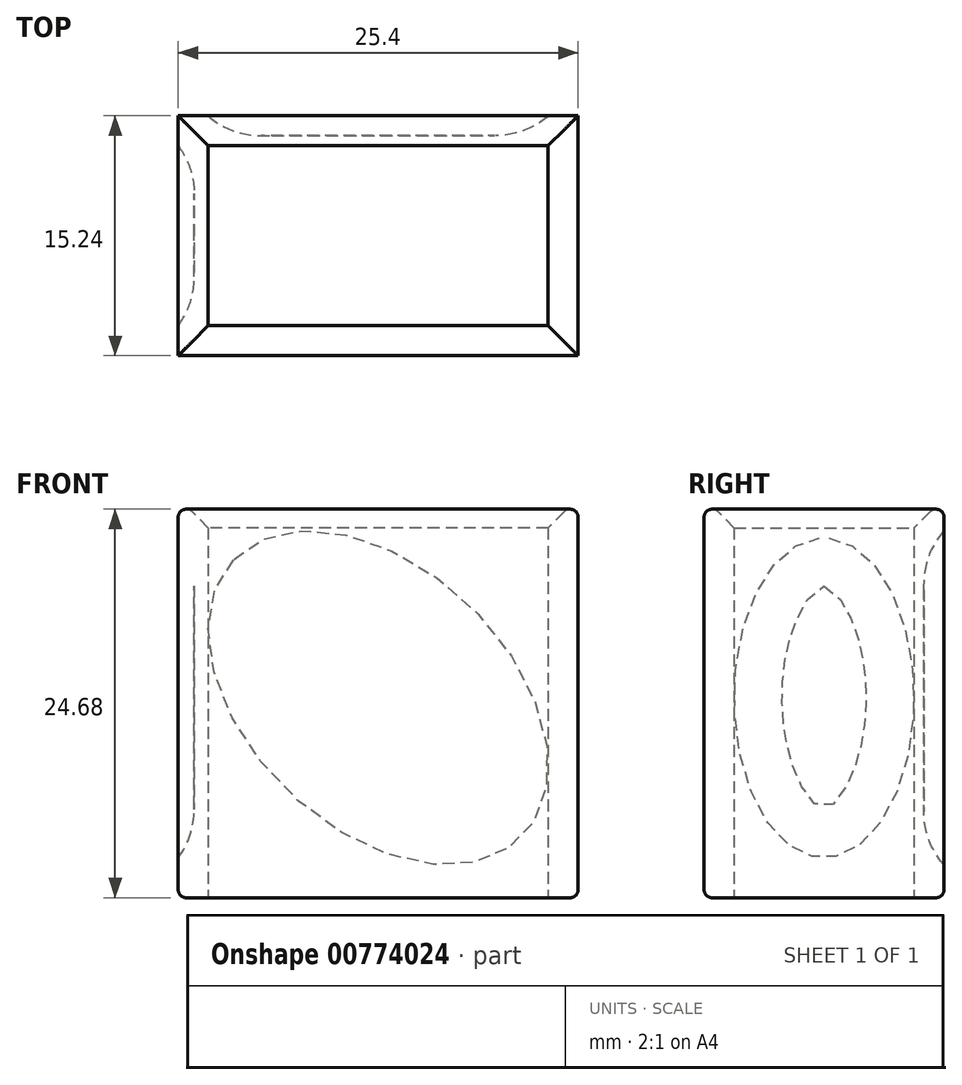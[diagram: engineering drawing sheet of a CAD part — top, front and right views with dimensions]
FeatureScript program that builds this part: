
annotation { "Feature Type Name" : "Feature", "Feature Type Description" : "" }
export const myFeature = defineFeature(function(context is Context, id is Id, definition is map)
    precondition{}
    {
        {
            var Q0;
            Q0=qCreatedBy(makeId("Top.planeOp"),FACE);
            var sketch = newSketch(context, id + "F0", { "sketchPlane" : qUnion([Q0])});
            skLineSegment(sketch, "E0.bottom", {"start": v(10.8, 5.72) * mm, "end": v(-10.8, 5.72) * mm});
            skLineSegment(sketch, "E0.top", {"start": v(10.8, -5.71) * mm, "end": v(-10.8, -5.71) * mm});
            skLineSegment(sketch, "E0.left", {"start": v(10.8, 5.72) * mm, "end": v(10.8, -5.71) * mm});
            skLineSegment(sketch, "E0.right", {"start": v(-10.8, 5.72) * mm, "end": v(-10.8, -5.72) * mm});
            skPoint(sketch, "E0.middle", {"position": v(0, 0) * mm});
            skLineSegment(sketch, "E1.0", {"start": v(12.7, 7.62) * mm, "end": v(-12.7, 7.62) * mm});
            skLineSegment(sketch, "E1.1", {"start": v(12.7, 7.62) * mm, "end": v(12.7, -7.62) * mm});
            skLineSegment(sketch, "E1.2", {"start": v(12.7, -7.62) * mm, "end": v(-12.7, -7.62) * mm});
            skLineSegment(sketch, "E1.3", {"start": v(-12.7, 7.62) * mm, "end": v(-12.7, -7.62) * mm});
            skSolve(sketch);
        }
        {
            var Q0;
            Q0=makeQuery(id+"F0.imprint","IMPRINT",FACE,{"disambiguationData":[TD([[makeQuery(id+"F0.imprint","IMPRINT",EDGE,{"derivedFrom":sQuery(id+"F0.wireOp",EDGE,"E0.bottom")}),-1.0]])]});
            extrude(context, id + "F1", {"entities" : qUnion([Q0]), "depth" : 25.4 * mm, "offsetDistance" : 25.4 * mm});
        }
        {
            var Q0;
            Q0=makeQuery(id+"F1.opExtrude","CAP_EDGE",EDGE,{"disambiguationData":[OSD([sQuery(id+"F0.wireOp",EDGE,"E0.right")])],"isStart":false});
            var Q1;
            Q1=makeQuery(id+"F1.opExtrude","CAP_EDGE",EDGE,{"disambiguationData":[OSD([sQuery(id+"F0.wireOp",EDGE,"E0.bottom")])],"isStart":false});
            var Q2;
            Q2=makeQuery(id+"F1.opExtrude","CAP_EDGE",EDGE,{"disambiguationData":[OSD([sQuery(id+"F0.wireOp",EDGE,"E0.top")])],"isStart":false});
            var Q3;
            Q3=makeQuery(id+"F1.opExtrude","CAP_EDGE",EDGE,{"disambiguationData":[OSD([sQuery(id+"F0.wireOp",EDGE,"E0.left")])],"isStart":false});
            chamfer(context, id + "F2", {"entities" : qUnion([Q0, Q1, Q2, Q3]), "width" : 1.9 * mm, "tangentPropagation" : true});
        }
        {
            var Q0;
            Q0=makeQuery(id+"F1.opExtrude","SWEPT_FACE",FACE,{"disambiguationData":[OSD([sQuery(id+"F0.wireOp",EDGE,"E1.3")])]});
            var sketch = newSketch(context, id + "F3", { "sketchPlane" : qUnion([Q0])});
            skEllipse(sketch, "E2", {"center": v(0, 12.7) * mm, "majorRadius": 10.16 * mm, "minorRadius": 5.72 * mm, "majorAxis": v(0, 1)});
            skPoint(sketch, "E3.orphan", {"position": v(-7.62, 12.7) * mm});
            skSolve(sketch);
        }
        {
            var Q0;
            Q0=makeQuery(id+"F3.imprint","IMPRINT",FACE,{"disambiguationData":[TD([[makeQuery(id+"F3.imprint","IMPRINT",EDGE,{"derivedFrom":sQuery(id+"F3.wireOp",EDGE,"E2")}),1.0]])]});
            extrude(context, id + "F4", {"entities" : qUnion([Q0]), "operationType" : NewBodyOperationType.REMOVE, "oppositeDirection" : true, "depth" : 1.02 * mm, "offsetDistance" : 25.4 * mm});
        }
        {
            var Q0;
            Q0=makeQuery(id+"F4.boolean.opBoolean","COPY",EDGE,{"derivedFrom":makeQuery(id+"F4.opExtrude","CAP_EDGE",EDGE,{"disambiguationData":[OSD([sQuery(id+"F3.wireOp",EDGE,"E2")])],"isStart":false})});
            fillet(context, id + "F5", {"entities" : qUnion([Q0]), "radius" : 5.08 * mm, "tangentPropagation" : true, "allowEdgeOverflow" : false});
        }
        {
            var Q0;
            Q0=makeQuery(id+"F1.opExtrude","SWEPT_FACE",FACE,{"disambiguationData":[OSD([sQuery(id+"F0.wireOp",EDGE,"E1.0")])]});
            var sketch = newSketch(context, id + "F6", { "sketchPlane" : qUnion([Q0])});
            skEllipse(sketch, "E4", {"center": v(0, 12.7) * mm, "majorRadius": 12.7 * mm, "minorRadius": 8.26 * mm, "majorAxis": v(0.72, 0.7)});
            skPoint(sketch, "E4.centerSnap0", {"position": v(12.7, 12.7) * mm});
            skSolve(sketch);
        }
        {
            var Q0;
            Q0=makeQuery(id+"F6.imprint","IMPRINT",FACE,{"disambiguationData":[TD([[makeQuery(id+"F6.imprint","IMPRINT",EDGE,{"derivedFrom":sQuery(id+"F6.wireOp",EDGE,"E4")}),1.0]])]});
            extrude(context, id + "F7", {"entities" : qUnion([Q0]), "operationType" : NewBodyOperationType.REMOVE, "oppositeDirection" : true, "depth" : 1.27 * mm, "offsetDistance" : 25.4 * mm});
        }
        {
            var Q0;
            Q0=makeQuery(id+"F7.boolean.opBoolean","COPY",EDGE,{"derivedFrom":makeQuery(id+"F7.opExtrude","CAP_EDGE",EDGE,{"disambiguationData":[OSD([sQuery(id+"F6.wireOp",EDGE,"E4")])],"isStart":false})});
            fillet(context, id + "F8", {"entities" : qUnion([Q0]), "radius" : 5.08 * mm, "tangentPropagation" : true, "allowEdgeOverflow" : false});
        }
        {
            var Q0;
            Q0=makeQuery(id+"F2.opChamfer","BLEND_EDGE",EDGE,{"blendedFrom":[makeQuery(id+"F1.opExtrude","CAP_EDGE",EDGE,{"disambiguationData":[OSD([sQuery(id+"F0.wireOp",EDGE,"E0.right")])],"isStart":false}),makeQuery(id+"F1.opExtrude","SWEPT_FACE",FACE,{"disambiguationData":[OSD([sQuery(id+"F0.wireOp",EDGE,"E1.3")])]})],"blendedInto":[makeQuery(id+"F1.opExtrude","SWEPT_FACE",FACE,{"disambiguationData":[OSD([sQuery(id+"F0.wireOp",EDGE,"E1.3")])]})]});
            var Q1;
            Q1=makeQuery(id+"F2.opChamfer","BLEND_EDGE",EDGE,{"blendedFrom":[makeQuery(id+"F1.opExtrude","CAP_EDGE",EDGE,{"disambiguationData":[OSD([sQuery(id+"F0.wireOp",EDGE,"E0.top")])],"isStart":false}),makeQuery(id+"F1.opExtrude","SWEPT_FACE",FACE,{"disambiguationData":[OSD([sQuery(id+"F0.wireOp",EDGE,"E1.2")])]})],"blendedInto":[makeQuery(id+"F1.opExtrude","SWEPT_FACE",FACE,{"disambiguationData":[OSD([sQuery(id+"F0.wireOp",EDGE,"E1.2")])]})]});
            var Q2;
            Q2=makeQuery(id+"F2.opChamfer","BLEND_EDGE",EDGE,{"blendedFrom":[makeQuery(id+"F1.opExtrude","CAP_EDGE",EDGE,{"disambiguationData":[OSD([sQuery(id+"F0.wireOp",EDGE,"E0.bottom")])],"isStart":false}),makeQuery(id+"F1.opExtrude","SWEPT_FACE",FACE,{"disambiguationData":[OSD([sQuery(id+"F0.wireOp",EDGE,"E1.0")])]})],"blendedInto":[makeQuery(id+"F1.opExtrude","SWEPT_FACE",FACE,{"disambiguationData":[OSD([sQuery(id+"F0.wireOp",EDGE,"E1.0")])]})]});
            var Q3;
            Q3=makeQuery(id+"F2.opChamfer","BLEND_EDGE",EDGE,{"blendedFrom":[makeQuery(id+"F1.opExtrude","CAP_EDGE",EDGE,{"disambiguationData":[OSD([sQuery(id+"F0.wireOp",EDGE,"E0.left")])],"isStart":false}),makeQuery(id+"F1.opExtrude","SWEPT_FACE",FACE,{"disambiguationData":[OSD([sQuery(id+"F0.wireOp",EDGE,"E1.1")])]})],"blendedInto":[makeQuery(id+"F1.opExtrude","SWEPT_FACE",FACE,{"disambiguationData":[OSD([sQuery(id+"F0.wireOp",EDGE,"E1.1")])]})]});
            var Q4;
            Q4=makeQuery(id+"F1.opExtrude","CAP_EDGE",EDGE,{"disambiguationData":[OSD([sQuery(id+"F0.wireOp",EDGE,"E1.2")])],"isStart":true});
            var Q5;
            Q5=makeQuery(id+"F1.opExtrude","CAP_EDGE",EDGE,{"disambiguationData":[OSD([sQuery(id+"F0.wireOp",EDGE,"E1.3")])],"isStart":true});
            var Q6;
            Q6=makeQuery(id+"F1.opExtrude","CAP_EDGE",EDGE,{"disambiguationData":[OSD([sQuery(id+"F0.wireOp",EDGE,"E1.0")])],"isStart":true});
            var Q7;
            Q7=makeQuery(id+"F1.opExtrude","CAP_EDGE",EDGE,{"disambiguationData":[OSD([sQuery(id+"F0.wireOp",EDGE,"E1.1")])],"isStart":true});
            fillet(context, id + "F9", {"entities" : qUnion([Q0, Q1, Q2, Q3, Q4, Q5, Q6, Q7]), "radius" : 0.5 * mm, "tangentPropagation" : true, "allowEdgeOverflow" : false});
        }
    });
